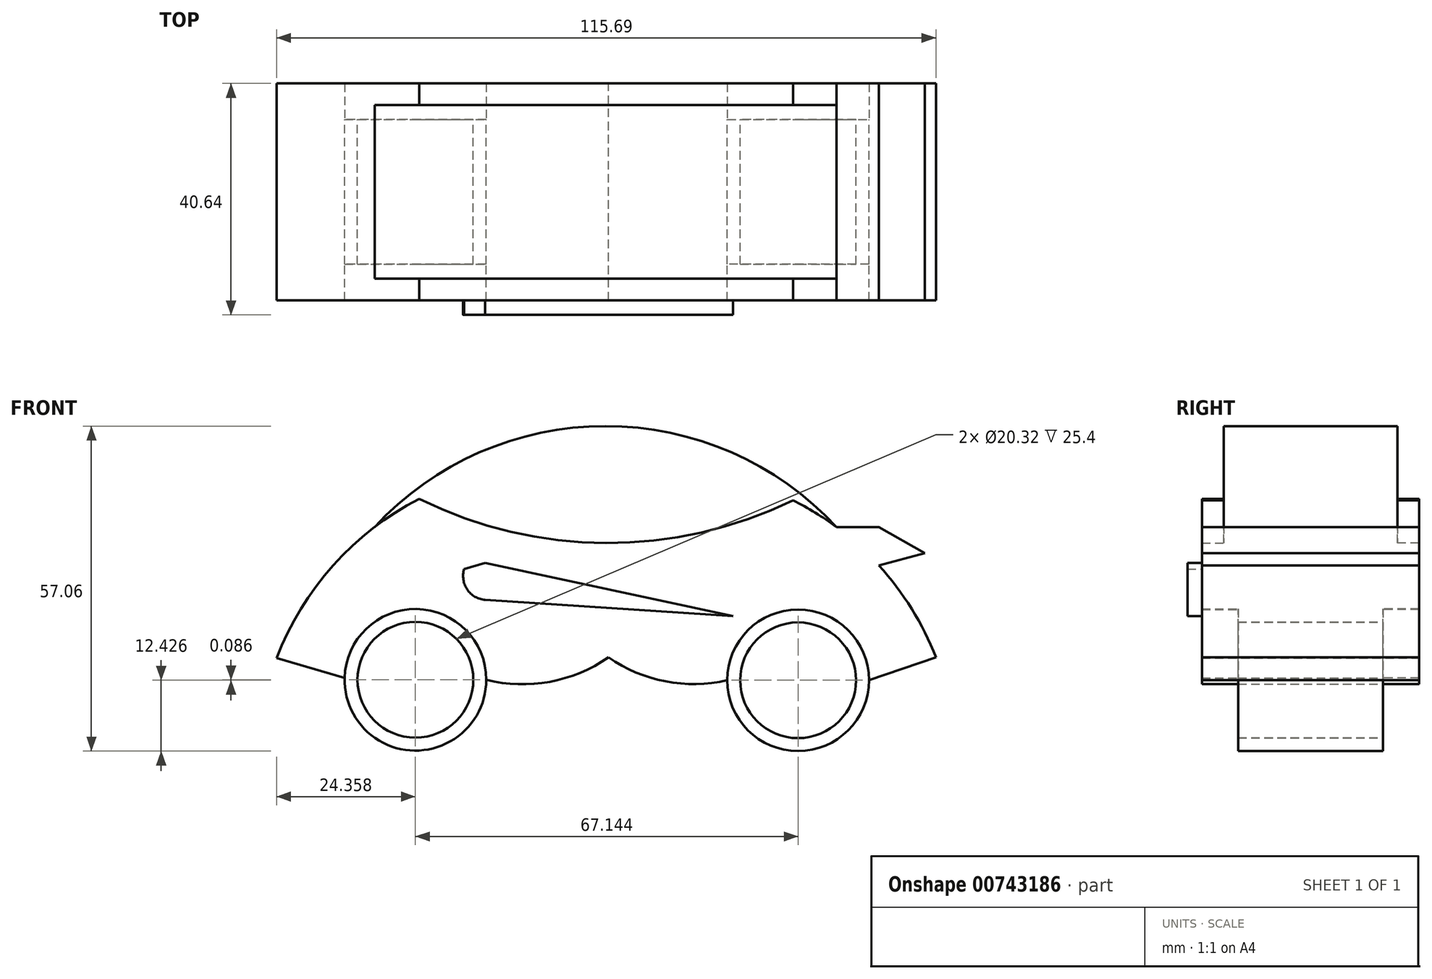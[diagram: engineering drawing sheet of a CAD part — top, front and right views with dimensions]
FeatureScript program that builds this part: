
annotation { "Feature Type Name" : "Feature", "Feature Type Description" : "" }
export const myFeature = defineFeature(function(context is Context, id is Id, definition is map)
    precondition{}
    {
        {
            var Q0;
            Q0=qCreatedBy(makeId("Front.planeOp"),FACE);
            var sketch = newSketch(context, id + "F0", { "sketchPlane" : qUnion([Q0])});
            skCircle(sketch, "E0", {"center": v(33.61, -26.9) * mm, "radius": 12.43 * mm});
            skCircle(sketch, "E1", {"center": v(-33.53, -26.82) * mm, "radius": 12.43 * mm});
            skArc(sketch, "E2", {"start": v(-21.1, -26.82) * mm, "mid": v(-9.96, -27.17) * mm, "end": v(0.33, -22.88) * mm});
            skArc(sketch, "E3", {"start": v(0.33, -22.88) * mm, "mid": v(10.33, -27.09) * mm, "end": v(21.18, -26.9) * mm});
            skLineSegment(sketch, "E4", {"start": v(-45.96, -26.5) * mm, "end": v(-57.89, -23.02) * mm});
            skArc(sketch, "E5", {"start": v(-32.87, 4.94) * mm, "mid": v(-47.97, -6.72) * mm, "end": v(-57.89, -23.02) * mm});
            skLineSegment(sketch, "E6", {"start": v(46.04, -26.9) * mm, "end": v(57.8, -22.88) * mm});
            skArc(sketch, "E7", {"start": v(57.8, -22.88) * mm, "mid": v(47.8, -6.77) * mm, "end": v(32.72, 4.7) * mm});
            skArc(sketch, "E8", {"start": v(-32.87, 4.94) * mm, "mid": v(-0.1, -2.81) * mm, "end": v(32.72, 4.7) * mm});
            skArc(sketch, "E9", {"start": v(40.33, 0) * mm, "mid": v(-0.18, 17.73) * mm, "end": v(-40.7, 0) * mm});
            skPoint(sketch, "E10.oppositeSnap0", {"position": v(47.8, -6.77) * mm});
            skLineSegment(sketch, "E10.bottom", {"start": v(40.33, 0) * mm, "end": v(29.88, 0) * mm});
            skLineSegment(sketch, "E10.top", {"start": v(40.33, -6.77) * mm, "end": v(29.88, -6.77) * mm});
            skLineSegment(sketch, "E10.right", {"start": v(29.88, 0) * mm, "end": v(29.88, -6.77) * mm});
            skLineSegment(sketch, "E11.bottom", {"start": v(40.33, -6.77) * mm, "end": v(47.8, -6.77) * mm});
            skLineSegment(sketch, "E11.top", {"start": v(40.33, 0) * mm, "end": v(47.8, 0) * mm});
            skLineSegment(sketch, "E11.right", {"start": v(47.8, -6.77) * mm, "end": v(47.8, 0) * mm});
            skCircle(sketch, "E12", {"center": v(-33.53, -26.82) * mm, "radius": 10.16 * mm});
            skCircle(sketch, "E13", {"center": v(33.61, -26.9) * mm, "radius": 10.16 * mm});
            skLineSegment(sketch, "E14", {"start": v(47.8, 0) * mm, "end": v(55.82, -4.58) * mm});
            skLineSegment(sketch, "E15", {"start": v(55.82, -4.58) * mm, "end": v(47.8, -6.77) * mm});
            skSolve(sketch);
        }
        {
            var Q0;
            {var subQ11=sQuery(id+"F0.wireOp",EDGE,"E2");Q0=makeQuery(id+"F0.imprint","IMPRINT",FACE,{"disambiguationData":[TD([[makeQuery(id+"F0.imprint","IMPRINT",EDGE,{"derivedFrom":subQ11}),1.0]])]});}
            extrude(context, id + "F1", {"entities" : qUnion([Q0]), "depth" : 19.05 * mm, "offsetDistance" : 25.4 * mm});
        }
        {
            var Q0;
            Q0=makeQuery(id+"F0.imprint","IMPRINT",FACE,{"disambiguationData":[TD([[makeQuery(id+"F0.imprint","IMPRINT",EDGE,{"derivedFrom":sQuery(id+"F0.wireOp",EDGE,"E12")}),-1.0]])]});
            var Q1;
            Q1=makeQuery(id+"F0.imprint","IMPRINT",FACE,{"disambiguationData":[TD([[makeQuery(id+"F0.imprint","IMPRINT",EDGE,{"derivedFrom":sQuery(id+"F0.wireOp",EDGE,"E13")}),-1.0]])]});
            extrude(context, id + "F2", {"entities" : qUnion([Q0, Q1]), "operationType" : NewBodyOperationType.ADD, "depth" : 12.7 * mm, "offsetDistance" : 25.4 * mm});
        }
        {
            var Q0;
            {var subQ0=sQuery(id+"F0.wireOp",EDGE,"E10.bottom");Q0=makeQuery(id+"F0.imprint","IMPRINT",FACE,{"disambiguationData":[TD([[makeQuery(id+"F0.imprint","IMPRINT",EDGE,{"derivedFrom":subQ0}),1.0]])]});}
            var Q1;
            {var subQ0=sQuery(id+"F0.wireOp",EDGE,"E11.top");Q1=makeQuery(id+"F0.imprint","IMPRINT",FACE,{"disambiguationData":[TD([[makeQuery(id+"F0.imprint","IMPRINT",EDGE,{"derivedFrom":subQ0}),-1.0]])]});}
            extrude(context, id + "F3", {"entities" : qUnion([Q0, Q1]), "operationType" : NewBodyOperationType.ADD, "depth" : 19.05 * mm, "offsetDistance" : 25.4 * mm});
        }
        {
            var Q0;
            Q0=makeQuery(id+"F0.imprint","IMPRINT",FACE,{"disambiguationData":[TD([[makeQuery(id+"F0.imprint","IMPRINT",EDGE,{"derivedFrom":sQuery(id+"F0.wireOp",EDGE,"E11.right")}),-1.0]])]});
            extrude(context, id + "F4", {"entities" : qUnion([Q0]), "operationType" : NewBodyOperationType.ADD, "depth" : 19.05 * mm, "offsetDistance" : 25.4 * mm});
        }
        {
            var Q0;
            {var subQ0=sQuery(id+"F0.wireOp",EDGE,"E8");Q0=makeQuery(id+"F0.imprint","IMPRINT",FACE,{"disambiguationData":[TD([[makeQuery(id+"F0.imprint","IMPRINT",EDGE,{"derivedFrom":subQ0}),1.0]])]});}
            extrude(context, id + "F5", {"entities" : qUnion([Q0]), "operationType" : NewBodyOperationType.ADD, "depth" : 15.24 * mm, "offsetDistance" : 25.4 * mm});
        }
        {
            var Q0;
            Q0=makeQuery(id+"F1.opExtrude","SWEPT_BODY",BODY,{"disambiguationData":[OSD([sQuery(id+"F0.wireOp",EDGE,"E0"),sQuery(id+"F0.wireOp",EDGE,"E1"),sQuery(id+"F0.wireOp",EDGE,"E2"),sQuery(id+"F0.wireOp",EDGE,"E3"),sQuery(id+"F0.wireOp",EDGE,"E4"),sQuery(id+"F0.wireOp",EDGE,"E5"),sQuery(id+"F0.wireOp",EDGE,"E6"),sQuery(id+"F0.wireOp",EDGE,"E7"),sQuery(id+"F0.wireOp",EDGE,"E8"),sQuery(id+"F0.wireOp",EDGE,"E10.bottom"),sQuery(id+"F0.wireOp",EDGE,"E10.top"),sQuery(id+"F0.wireOp",EDGE,"E10.right"),sQuery(id+"F0.wireOp",EDGE,"E11.bottom")])]});
            var Q1;
            Q1=qCreatedBy(makeId("Front.planeOp"),FACE);
            mirror(context, id + "F6", {"operationType" : NewBodyOperationType.ADD, "entities" : qUnion([Q0]), "mirrorPlane" : qUnion([Q1])});
        }
        {
            var Q0;
            {var subQ0=sQuery(id+"F0.wireOp",EDGE,"E11.right");var subQ1=sQuery(id+"F0.wireOp",EDGE,"E11.bottom");var subQ2=sQuery(id+"F0.wireOp",EDGE,"E10.right");var subQ3=sQuery(id+"F0.wireOp",EDGE,"E10.top");var subQ4=sQuery(id+"F0.wireOp",EDGE,"E10.bottom");Q0=makeQuery(id+"F4.boolean.opBoolean","MERGE",FACE,{"derivedFrom":[makeQuery(id+"F3.boolean.opBoolean","MERGE",FACE,{"derivedFrom":[makeQuery(id+"F1.opExtrude","CAP_FACE",FACE,{"disambiguationData":[OSD([sQuery(id+"F0.wireOp",EDGE,"E0"),sQuery(id+"F0.wireOp",EDGE,"E1"),sQuery(id+"F0.wireOp",EDGE,"E2"),sQuery(id+"F0.wireOp",EDGE,"E3"),sQuery(id+"F0.wireOp",EDGE,"E4"),sQuery(id+"F0.wireOp",EDGE,"E5"),sQuery(id+"F0.wireOp",EDGE,"E6"),sQuery(id+"F0.wireOp",EDGE,"E7"),sQuery(id+"F0.wireOp",EDGE,"E8"),subQ4,subQ3,subQ2,subQ1])],"isStart":false}),makeQuery(id+"F3.opExtrude","CAP_FACE",FACE,{"disambiguationData":[OSD([subQ4,subQ3,subQ2,subQ1,sQuery(id+"F0.wireOp",EDGE,"E11.top"),subQ0])],"isStart":false})]}),makeQuery(id+"F4.opExtrude","CAP_FACE",FACE,{"disambiguationData":[OSD([subQ0,sQuery(id+"F0.wireOp",EDGE,"E14"),sQuery(id+"F0.wireOp",EDGE,"E15")])],"isStart":false})]});}
            var sketch = newSketch(context, id + "F7", { "sketchPlane" : qUnion([Q0])});
            skLineSegment(sketch, "E16", {"start": v(-21.28, -6.3) * mm, "end": v(22.18, -15.66) * mm});
            skLineSegment(sketch, "E17", {"start": v(-21.28, -12.78) * mm, "end": v(22.18, -15.66) * mm});
            skArc(sketch, "E18", {"start": v(-24.97, -7.37) * mm, "mid": v(-24.44, -10.98) * mm, "end": v(-21.28, -12.78) * mm});
            skLineSegment(sketch, "E19", {"start": v(-24.97, -7.37) * mm, "end": v(-21.28, -6.3) * mm});
            skSolve(sketch);
        }
        {
            var Q0;
            Q0=makeQuery(id+"F7.imprint","IMPRINT",FACE,{"disambiguationData":[TD([[makeQuery(id+"F7.imprint","IMPRINT",EDGE,{"derivedFrom":sQuery(id+"F7.wireOp",EDGE,"E16")}),-1.0]])]});
            extrude(context, id + "F8", {"entities" : qUnion([Q0]), "operationType" : NewBodyOperationType.ADD, "depth" : 2.54 * mm, "offsetDistance" : 25.4 * mm});
        }
    });
